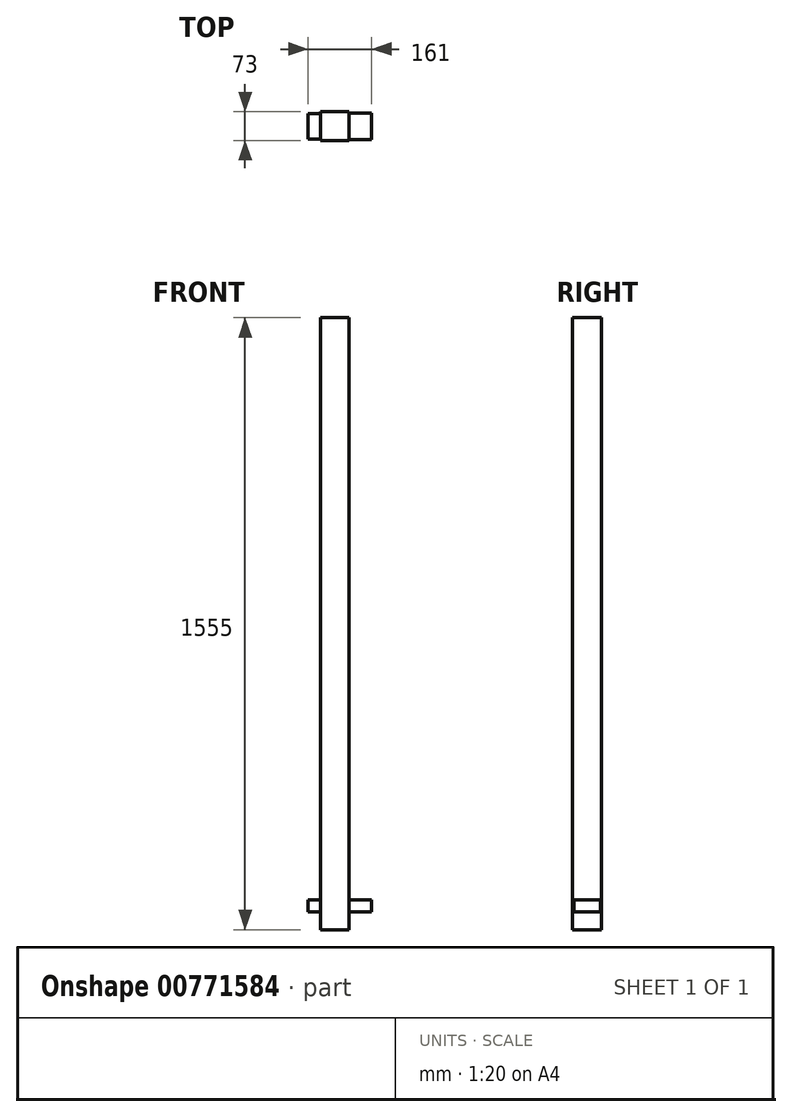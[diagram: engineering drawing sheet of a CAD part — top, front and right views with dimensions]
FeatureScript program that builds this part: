
annotation { "Feature Type Name" : "Feature", "Feature Type Description" : "" }
export const myFeature = defineFeature(function(context is Context, id is Id, definition is map)
    precondition{}
    {
        {
            var Q0;
            Q0=qCreatedBy(makeId("Top.planeOp"),FACE);
            var sketch = newSketch(context, id + "F0", { "sketchPlane" : qUnion([Q0])});
            skLineSegment(sketch, "E0.bottom", {"start": v(36.5, 36.5) * mm, "end": v(-36.5, 36.5) * mm});
            skLineSegment(sketch, "E0.top", {"start": v(36.5, -36.5) * mm, "end": v(-36.5, -36.5) * mm});
            skLineSegment(sketch, "E0.left", {"start": v(36.5, 36.5) * mm, "end": v(36.5, -36.5) * mm});
            skLineSegment(sketch, "E0.right", {"start": v(-36.5, 36.5) * mm, "end": v(-36.5, -36.5) * mm});
            skPoint(sketch, "E0.middle", {"position": v(0, 0) * mm});
            skSolve(sketch);
        }
        {
            var Q0;
            Q0=makeQuery(id+"F0.imprint","IMPRINT",FACE,{"disambiguationData":[TD([[makeQuery(id+"F0.imprint","IMPRINT",EDGE,{"derivedFrom":sQuery(id+"F0.wireOp",EDGE,"E0.bottom")}),1.0]])]});
            extrude(context, id + "F1", {"entities" : qUnion([Q0]), "depth" : 1555 * mm, "offsetDistance" : 25 * mm});
        }
        {
            var Q0;
            Q0=makeQuery(id+"F1.opExtrude","SWEPT_FACE",FACE,{"disambiguationData":[OSD([sQuery(id+"F0.wireOp",EDGE,"E0.right")])]});
            var sketch = newSketch(context, id + "F2", { "sketchPlane" : qUnion([Q0])});
            skLineSegment(sketch, "E1.bottom", {"start": v(-32.5, 76) * mm, "end": v(32.5, 76) * mm});
            skLineSegment(sketch, "E1.top", {"start": v(-32.5, 45) * mm, "end": v(32.5, 45) * mm});
            skLineSegment(sketch, "E1.left", {"start": v(-32.5, 76) * mm, "end": v(-32.5, 45) * mm});
            skLineSegment(sketch, "E1.right", {"start": v(32.5, 76) * mm, "end": v(32.5, 45) * mm});
            skPoint(sketch, "E1.middle", {"position": v(0, 60.5) * mm});
            skSolve(sketch);
        }
        {
            var Q0;
            Q0=makeQuery(id+"F2.imprint","IMPRINT",FACE,{"disambiguationData":[TD([[makeQuery(id+"F2.imprint","IMPRINT",EDGE,{"derivedFrom":sQuery(id+"F2.wireOp",EDGE,"E1.bottom")}),-1.0]])]});
            extrude(context, id + "F3", {"entities" : qUnion([Q0]), "operationType" : NewBodyOperationType.ADD, "depth" : 31 * mm, "offsetDistance" : 25 * mm});
        }
        {
            var Q0;
            Q0=makeQuery(id+"F1.opExtrude","SWEPT_FACE",FACE,{"disambiguationData":[OSD([sQuery(id+"F0.wireOp",EDGE,"E0.left")])]});
            var sketch = newSketch(context, id + "F4", { "sketchPlane" : qUnion([Q0])});
            skLineSegment(sketch, "E2.bottom", {"start": v(33.5, 45) * mm, "end": v(-33.5, 45) * mm});
            skLineSegment(sketch, "E2.top", {"start": v(33.5, 76) * mm, "end": v(-33.5, 76) * mm});
            skLineSegment(sketch, "E2.left", {"start": v(33.5, 45) * mm, "end": v(33.5, 76) * mm});
            skLineSegment(sketch, "E2.right", {"start": v(-33.5, 45) * mm, "end": v(-33.5, 76) * mm});
            skPoint(sketch, "E2.middle", {"position": v(0, 60.5) * mm});
            skSolve(sketch);
        }
        {
            var Q0;
            Q0=makeQuery(id+"F4.imprint","IMPRINT",FACE,{"disambiguationData":[TD([[makeQuery(id+"F4.imprint","IMPRINT",EDGE,{"derivedFrom":sQuery(id+"F4.wireOp",EDGE,"E2.bottom")}),-1.0]])]});
            extrude(context, id + "F5", {"entities" : qUnion([Q0]), "operationType" : NewBodyOperationType.ADD, "depth" : 57 * mm, "offsetDistance" : 25 * mm});
        }
    });
